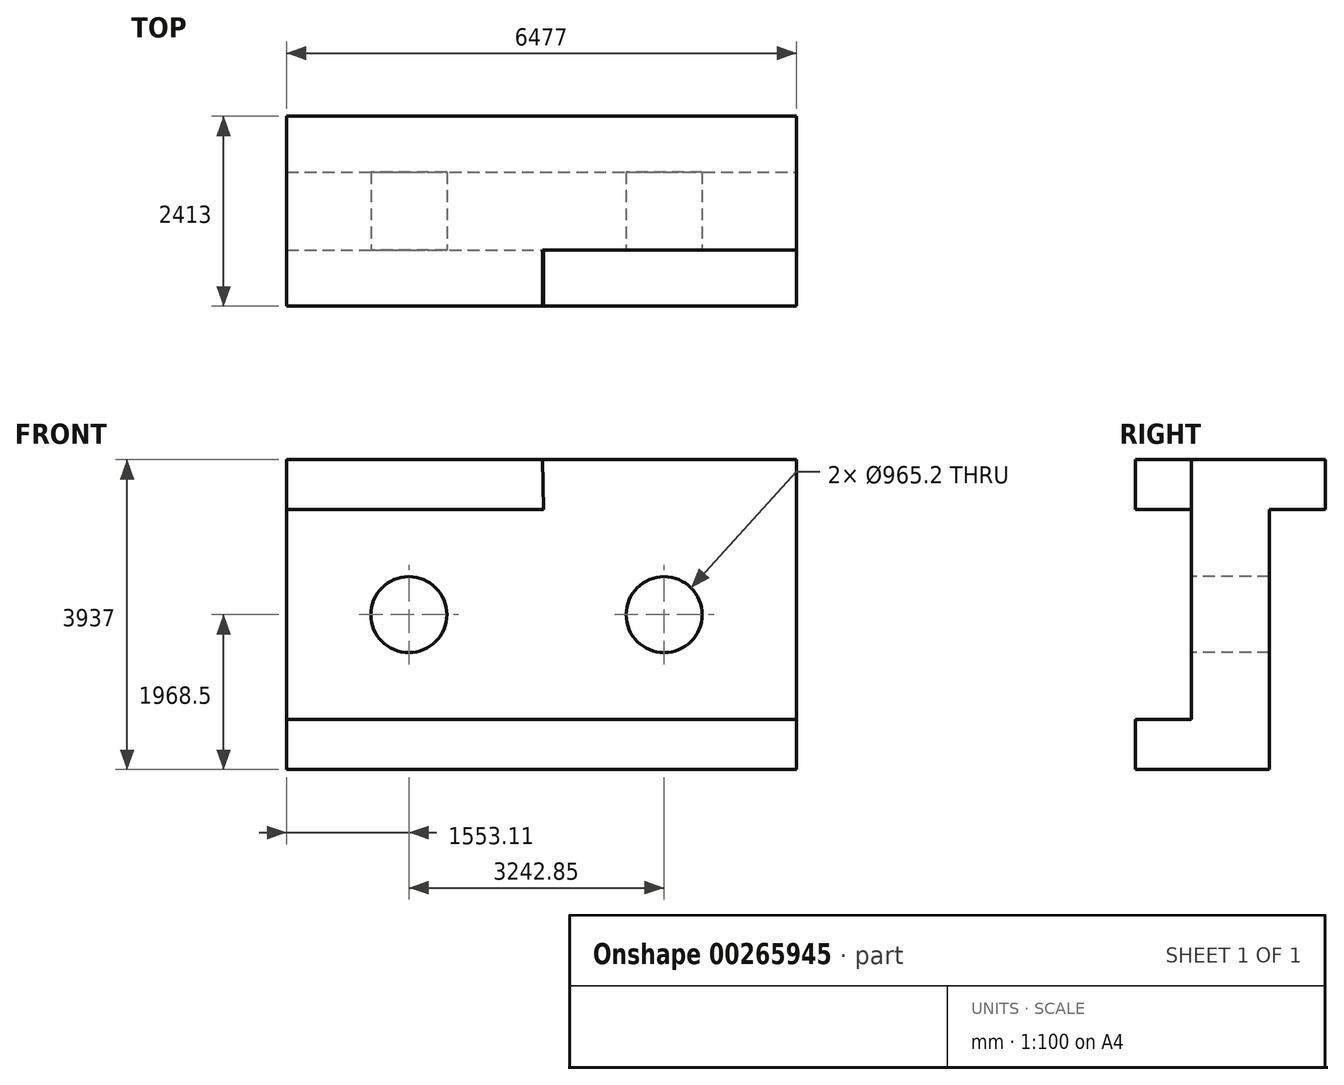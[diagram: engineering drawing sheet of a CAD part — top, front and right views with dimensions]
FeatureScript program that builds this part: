
annotation { "Feature Type Name" : "Feature", "Feature Type Description" : "" }
export const myFeature = defineFeature(function(context is Context, id is Id, definition is map)
    precondition{}
    {
        {
            var Q0;
            Q0=qCreatedBy(makeId("Front.planeOp"),FACE);
            var sketch = newSketch(context, id + "F0", { "sketchPlane" : qUnion([Q0])});
            skLineSegment(sketch, "E0", {"start": v(-3263.28, -56.4) * mm, "end": v(3213.72, -56.4) * mm});
            skLineSegment(sketch, "E1", {"start": v(-3263.28, -56.4) * mm, "end": v(-3263.28, 3880.6) * mm});
            skLineSegment(sketch, "E2", {"start": v(-3263.28, 3880.6) * mm, "end": v(3213.72, 3880.6) * mm});
            skLineSegment(sketch, "E3", {"start": v(3213.72, 3880.6) * mm, "end": v(3213.72, -56.4) * mm});
            skSolve(sketch);
        }
        {
            var Q0;
            Q0 = qSketchRegion(id + "F0", true);
            extrude(context, id + "F1", {"entities" : qUnion([Q0]), "depth" : 2413 * mm});
        }
        {
            var Q0;
            Q0=makeQuery(id+"F1.opExtrude","CAP_FACE",FACE,{"disambiguationData":[OSD([sQuery(id+"F0.wireOp",EDGE,"E0"),sQuery(id+"F0.wireOp",EDGE,"E1"),sQuery(id+"F0.wireOp",EDGE,"E2"),sQuery(id+"F0.wireOp",EDGE,"E3")])],"isStart":false});
            var sketch = newSketch(context, id + "F2", { "sketchPlane" : qUnion([Q0])});
            skLineSegment(sketch, "E4", {"start": v(3213.72, 3880.6) * mm, "end": v(-12.08, 3880.6) * mm});
            skLineSegment(sketch, "E5", {"start": v(-3263.28, 3245.6) * mm, "end": v(0, 3245.6) * mm});
            skLineSegment(sketch, "E6", {"start": v(0, 3245.6) * mm, "end": v(-12.08, 3880.6) * mm});
            skLineSegment(sketch, "E7", {"start": v(-3263.28, -56.4) * mm, "end": v(-3263.28, 578.6) * mm});
            skLineSegment(sketch, "E8", {"start": v(-3263.28, 578.6) * mm, "end": v(3213.72, 578.6) * mm});
            skCircle(sketch, "E9", {"center": v(-1710.17, 1912.1) * mm, "radius": 482.6 * mm});
            skPoint(sketch, "E9.centerSnap0", {"position": v(-3263.28, 1912.1) * mm});
            skCircle(sketch, "E10", {"center": v(1532.68, 1912.1) * mm, "radius": 482.6 * mm});
            skSolve(sketch);
        }
        {
            var Q0;
            {var subQ3=sQuery(id+"F2.wireOp",EDGE,"E4");Q0=makeQuery(id+"F2.imprint","IMPRINT",FACE,{"disambiguationData":[TD([[makeQuery(id+"F2.imprint","IMPRINT",EDGE,{"derivedFrom":subQ3}),-1.0]])]});}
            extrude(context, id + "F3", {"entities" : qUnion([Q0]), "operationType" : NewBodyOperationType.REMOVE, "oppositeDirection" : true, "depth" : 711.2 * mm});
        }
        {
            var Q0;
            Q0=makeQuery(id+"F3.boolean.opBoolean","SPLIT",FACE,{"disambiguationData":[TD([makeQuery(id+"F3.opExtrude","SWEPT_FACE",FACE,{"disambiguationData":[OSD([sQuery(id+"F2.wireOp",EDGE,"E9")])]})])],"derivedFrom":makeQuery(id+"F1.opExtrude","CAP_FACE",FACE,{"disambiguationData":[OSD([sQuery(id+"F0.wireOp",EDGE,"E0"),sQuery(id+"F0.wireOp",EDGE,"E1"),sQuery(id+"F0.wireOp",EDGE,"E2"),sQuery(id+"F0.wireOp",EDGE,"E3")])],"isStart":false})});
            var Q1;
            Q1=makeQuery(id+"F3.boolean.opBoolean","SPLIT",FACE,{"disambiguationData":[TD([makeQuery(id+"F3.opExtrude","SWEPT_FACE",FACE,{"disambiguationData":[OSD([sQuery(id+"F2.wireOp",EDGE,"E10")])]})])],"derivedFrom":makeQuery(id+"F1.opExtrude","CAP_FACE",FACE,{"disambiguationData":[OSD([sQuery(id+"F0.wireOp",EDGE,"E0"),sQuery(id+"F0.wireOp",EDGE,"E1"),sQuery(id+"F0.wireOp",EDGE,"E2"),sQuery(id+"F0.wireOp",EDGE,"E3")])],"isStart":false})});
            extrude(context, id + "F4", {"entities" : qUnion([Q0, Q1]), "operationType" : NewBodyOperationType.REMOVE, "oppositeDirection" : true, "depth" : 1701.8 * mm});
        }
        {
            var Q0;
            Q0=makeQuery(id+"F1.opExtrude","CAP_FACE",FACE,{"disambiguationData":[OSD([sQuery(id+"F0.wireOp",EDGE,"E0"),sQuery(id+"F0.wireOp",EDGE,"E1"),sQuery(id+"F0.wireOp",EDGE,"E2"),sQuery(id+"F0.wireOp",EDGE,"E3")])],"isStart":true});
            var sketch = newSketch(context, id + "F5", { "sketchPlane" : qUnion([Q0])});
            skLineSegment(sketch, "E11", {"start": v(3263.28, 3880.6) * mm, "end": v(3263.28, 3245.6) * mm});
            skLineSegment(sketch, "E12", {"start": v(3263.28, 3245.6) * mm, "end": v(3263.28, -56.4) * mm});
            skLineSegment(sketch, "E13", {"start": v(3263.28, -56.4) * mm, "end": v(3263.28, 578.6) * mm});
            skLineSegment(sketch, "E14", {"start": v(3263.28, 578.6) * mm, "end": v(-3213.72, 578.6) * mm});
            skLineSegment(sketch, "E15", {"start": v(-3213.72, 578.6) * mm, "end": v(3263.28, 578.6) * mm});
            skLineSegment(sketch, "E16", {"start": v(3263.28, 3245.6) * mm, "end": v(-3213.72, 3245.6) * mm});
            skSolve(sketch);
        }
        {
            var Q0;
            Q0 = qSketchRegion(id + "F5", true);
            var Q1;
            Q1=makeQuery(id+"F5.imprint","IMPRINT",FACE,{"disambiguationData":[TD([[makeQuery(id+"F5.imprint","IMPRINT",EDGE,{"derivedFrom":sQuery(id+"F5.wireOp",EDGE,"E12")}),1.0]])]});
            extrude(context, id + "F6", {"entities" : qUnion([Q0, Q1]), "operationType" : NewBodyOperationType.REMOVE, "oppositeDirection" : true, "depth" : 711.2 * mm});
        }
    });
